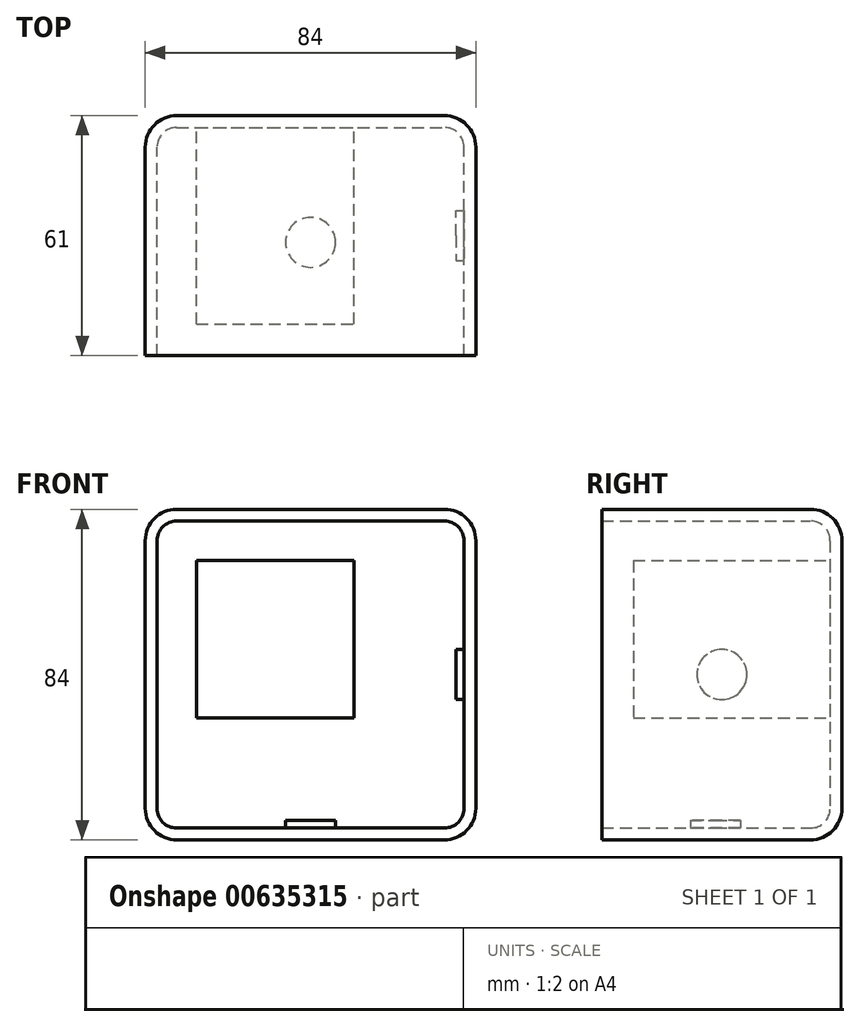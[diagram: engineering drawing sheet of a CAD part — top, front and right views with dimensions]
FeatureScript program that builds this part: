
annotation { "Feature Type Name" : "Feature", "Feature Type Description" : "" }
export const myFeature = defineFeature(function(context is Context, id is Id, definition is map)
    precondition{}
    {
        {
            var Q0;
            Q0=qCreatedBy(makeId("Top.planeOp"),FACE);
            var sketch = newSketch(context, id + "F0", { "sketchPlane" : qUnion([Q0])});
            skLineSegment(sketch, "E0.bottom", {"start": v(42, 30.5) * mm, "end": v(-42, 30.5) * mm});
            skLineSegment(sketch, "E0.top", {"start": v(42, -30.5) * mm, "end": v(-42, -30.5) * mm});
            skLineSegment(sketch, "E0.left", {"start": v(42, 30.5) * mm, "end": v(42, -30.5) * mm});
            skLineSegment(sketch, "E0.right", {"start": v(-42, 30.5) * mm, "end": v(-42, -30.5) * mm});
            skPoint(sketch, "E0.middle", {"position": v(0, 0) * mm});
            skSolve(sketch);
        }
        {
            var Q0;
            Q0=makeQuery(id+"F0.imprint","IMPRINT",FACE,{"disambiguationData":[TD([[makeQuery(id+"F0.imprint","IMPRINT",EDGE,{"derivedFrom":sQuery(id+"F0.wireOp",EDGE,"E0.bottom")}),1.0]])]});
            extrude(context, id + "F1", {"entities" : qUnion([Q0]), "depth" : 84 * mm, "offsetDistance" : 25.4 * mm});
        }
        {
            var Q0;
            Q0=makeQuery(id+"F1.opExtrude","CAP_EDGE",EDGE,{"disambiguationData":[OSD([sQuery(id+"F0.wireOp",EDGE,"E0.right")])],"isStart":false});
            var Q1;
            Q1=makeQuery(id+"F1.opExtrude","SWEPT_EDGE",EDGE,{"disambiguationData":[OSD([sQuery(id+"F0.wireOp",EDGE,"E0.bottom"),sQuery(id+"F0.wireOp",EDGE,"E0.right")])]});
            var Q2;
            Q2=makeQuery(id+"F1.opExtrude","CAP_EDGE",EDGE,{"disambiguationData":[OSD([sQuery(id+"F0.wireOp",EDGE,"E0.bottom")])],"isStart":false});
            var Q3;
            Q3=makeQuery(id+"F1.opExtrude","CAP_EDGE",EDGE,{"disambiguationData":[OSD([sQuery(id+"F0.wireOp",EDGE,"E0.bottom")])],"isStart":true});
            var Q4;
            Q4=makeQuery(id+"F1.opExtrude","CAP_EDGE",EDGE,{"disambiguationData":[OSD([sQuery(id+"F0.wireOp",EDGE,"E0.right")])],"isStart":true});
            var Q5;
            Q5=makeQuery(id+"F1.opExtrude","CAP_EDGE",EDGE,{"disambiguationData":[OSD([sQuery(id+"F0.wireOp",EDGE,"E0.left")])],"isStart":false});
            var Q6;
            Q6=makeQuery(id+"F1.opExtrude","SWEPT_EDGE",EDGE,{"disambiguationData":[OSD([sQuery(id+"F0.wireOp",EDGE,"E0.bottom"),sQuery(id+"F0.wireOp",EDGE,"E0.left")])]});
            var Q7;
            Q7=makeQuery(id+"F1.opExtrude","CAP_EDGE",EDGE,{"disambiguationData":[OSD([sQuery(id+"F0.wireOp",EDGE,"E0.left")])],"isStart":true});
            fillet(context, id + "F2", {"entities" : qUnion([Q0, Q1, Q2, Q3, Q4, Q5, Q6, Q7]), "radius" : 8 * mm, "tangentPropagation" : true, "allowEdgeOverflow" : false});
        }
        {
            var Q0;
            Q0=makeQuery(id+"F1.opExtrude","SWEPT_FACE",FACE,{"disambiguationData":[OSD([sQuery(id+"F0.wireOp",EDGE,"E0.top")])]});
            shell(context, id + "F3", {"entities" : qUnion([Q0]), "thickness" : 3 * mm});
        }
        {
            var Q0;
            {var subQ0=sQuery(id+"F0.wireOp",EDGE,"E0.right");var subQ1=sQuery(id+"F0.wireOp",EDGE,"E0.left");var subQ2=sQuery(id+"F0.wireOp",EDGE,"E0.top");var subQ3=sQuery(id+"F0.wireOp",EDGE,"E0.bottom");Q0=makeQuery(id+"F3.opShell","OFFSET_FACE",FACE,{"disambiguationData":[OSD([subQ3,subQ2,subQ1,subQ0]),TDD([makeQuery(id+"F1.opExtrude","CAP_FACE",FACE,{"disambiguationData":[OSD([subQ3,subQ2,subQ1,subQ0])],"isStart":true})])]});}
            var sketch = newSketch(context, id + "F4", { "sketchPlane" : qUnion([Q0])});
            skCircle(sketch, "E1", {"center": v(0, -1.68) * mm, "radius": 6.35 * mm});
            skSolve(sketch);
        }
        {
            var Q0;
            Q0 = qSketchRegion(id + "F4", true);
            extrude(context, id + "F5", {"entities" : qUnion([Q0]), "operationType" : NewBodyOperationType.ADD, "depth" : 2 * mm, "offsetDistance" : 25.4 * mm});
        }
        {
            var Q0;
            {var subQ0=sQuery(id+"F0.wireOp",EDGE,"E0.left");Q0=makeQuery(id+"F3.opShell","OFFSET_FACE",FACE,{"disambiguationData":[OSD([subQ0]),TDD([makeQuery(id+"F1.opExtrude","SWEPT_FACE",FACE,{"disambiguationData":[OSD([subQ0])]})])]});}
            var sketch = newSketch(context, id + "F6", { "sketchPlane" : qUnion([Q0])});
            skPoint(sketch, "E2.0", {"position": v(0, 0) * mm});
            skLineSegment(sketch, "E3", {"start": v(0, 0) * mm, "end": v(0, 84) * mm, "construction": true});
            skCircle(sketch, "E4", {"center": v(0, 42) * mm, "radius": 6.35 * mm});
            skSolve(sketch);
        }
        {
            var Q0;
            Q0=makeQuery(id+"F6.imprint","IMPRINT",FACE,{"disambiguationData":[TD([[makeQuery(id+"F6.imprint","IMPRINT",EDGE,{"derivedFrom":sQuery(id+"F6.wireOp",EDGE,"E4")}),1.0]])]});
            extrude(context, id + "F7", {"entities" : qUnion([Q0]), "operationType" : NewBodyOperationType.ADD, "depth" : 2 * mm, "offsetDistance" : 25.4 * mm});
        }
        {
            var Q0;
            {var subQ0=sQuery(id+"F0.wireOp",EDGE,"E0.bottom");Q0=makeQuery(id+"F3.opShell","OFFSET_FACE",FACE,{"disambiguationData":[OSD([subQ0]),TDD([makeQuery(id+"F1.opExtrude","SWEPT_FACE",FACE,{"disambiguationData":[OSD([subQ0])]})])]});}
            var sketch = newSketch(context, id + "F8", { "sketchPlane" : qUnion([Q0])});
            skLineSegment(sketch, "E5.bottom", {"start": v(-29, 71) * mm, "end": v(11, 71) * mm});
            skLineSegment(sketch, "E5.top", {"start": v(-29, 31) * mm, "end": v(11, 31) * mm});
            skLineSegment(sketch, "E5.left", {"start": v(-29, 71) * mm, "end": v(-29, 31) * mm});
            skLineSegment(sketch, "E5.right", {"start": v(11, 71) * mm, "end": v(11, 31) * mm});
            skSolve(sketch);
        }
        {
            var Q0;
            Q0=makeQuery(id+"F8.imprint","IMPRINT",FACE,{"disambiguationData":[TD([[makeQuery(id+"F8.imprint","IMPRINT",EDGE,{"derivedFrom":sQuery(id+"F8.wireOp",EDGE,"E5.bottom")}),-1.0]])]});
            var Q1;
            Q1=makeQuery(id+"F1.opExtrude","SWEPT_FACE",FACE,{"disambiguationData":[OSD([sQuery(id+"F0.wireOp",EDGE,"E0.top")])]});
            extrude(context, id + "F9", {"entities" : qUnion([Q0]), "operationType" : NewBodyOperationType.ADD, "depth" : 50 * mm, "offsetDistance" : 25.4 * mm});
        }
    });
